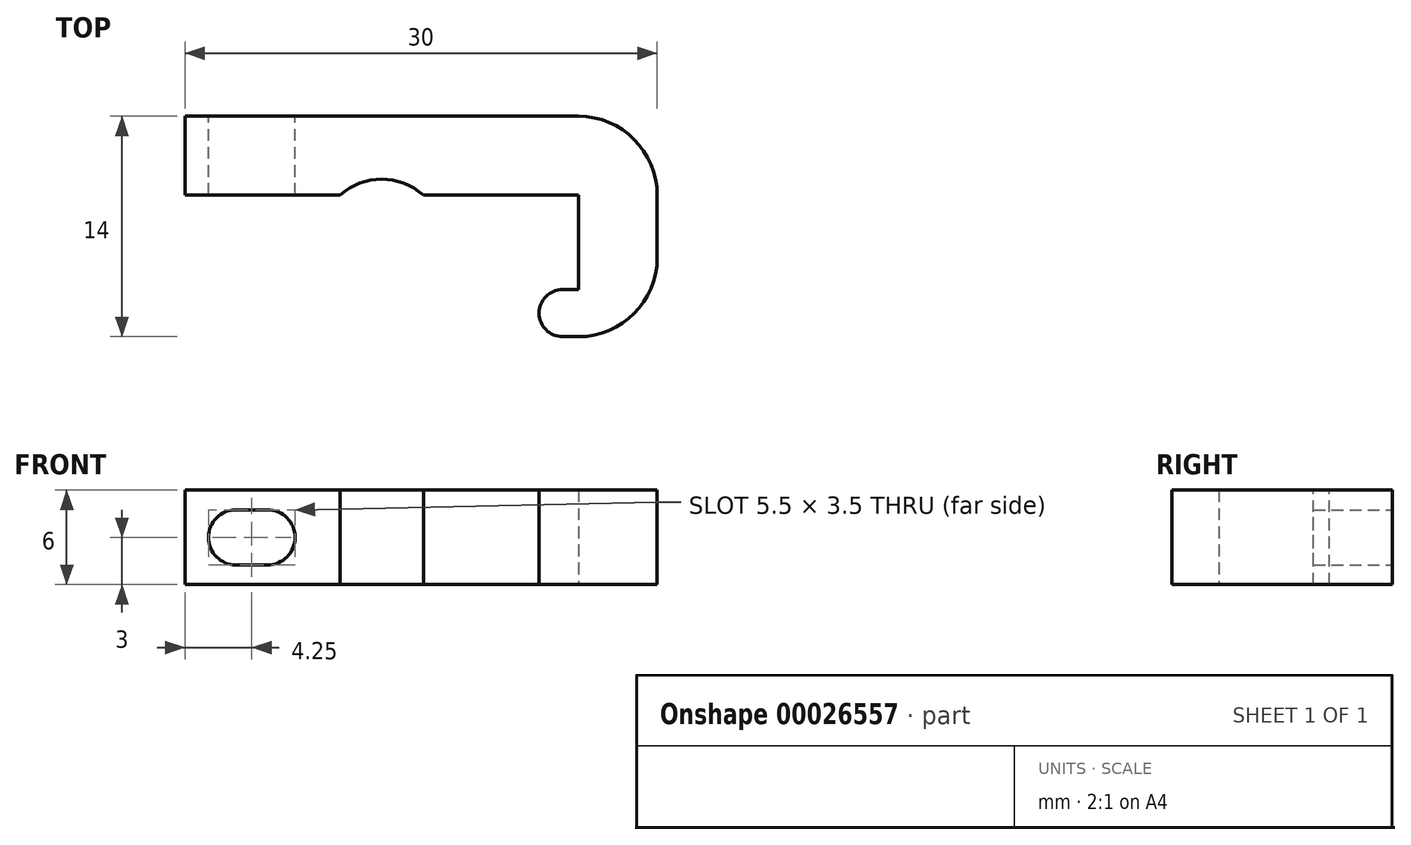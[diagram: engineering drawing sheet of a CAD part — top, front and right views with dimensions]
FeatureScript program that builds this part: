
annotation { "Feature Type Name" : "Feature", "Feature Type Description" : "" }
export const myFeature = defineFeature(function(context is Context, id is Id, definition is map)
    precondition{}
    {
        {
            var Q0;
            Q0=qCreatedBy(makeId("Top.planeOp"),FACE);
            var sketch = newSketch(context, id + "F0", { "sketchPlane" : qUnion([Q0])});
            skLineSegment(sketch, "E0", {"start": v(0, 0) * mm, "end": v(5, 0) * mm});
            skLineSegment(sketch, "E1", {"start": v(5, 0) * mm, "end": v(5, 14) * mm});
            skLineSegment(sketch, "E2", {"start": v(5, 14) * mm, "end": v(-25, 14) * mm});
            skLineSegment(sketch, "E3", {"start": v(-25, 14) * mm, "end": v(-25, 9) * mm});
            skLineSegment(sketch, "E4", {"start": v(-25, 9) * mm, "end": v(0, 9) * mm});
            skLineSegment(sketch, "E5", {"start": v(0, 9) * mm, "end": v(0, 3) * mm});
            skLineSegment(sketch, "E6", {"start": v(0, 3) * mm, "end": v(-1, 3) * mm});
            skLineSegment(sketch, "E7", {"start": v(0, 0) * mm, "end": v(-1, 0) * mm});
            skArc(sketch, "E8", {"start": v(-1, 3) * mm, "mid": v(-2.5, 1.5) * mm, "end": v(-1, 0) * mm});
            skSolve(sketch);
        }
        {
            var Q0;
            Q0=qSketchRegion(id+"F0",true);
            extrude(context, id + "F1", {"entities" : qUnion([Q0]), "depth" : 6 * mm});
        }
        {
            var Q0;
            Q0=makeQuery(id+"F1.opExtrude","SWEPT_FACE",FACE,{"disambiguationData":[OSD([sQuery(id+"F0.wireOp",EDGE,"E2")])]});
            var sketch = newSketch(context, id + "F2", { "sketchPlane" : qUnion([Q0])});
            skCircle(sketch, "E9", {"center": v(21.75, 3) * mm, "radius": 1.75 * mm});
            skLineSegment(sketch, "E10", {"start": v(21.75, 6) * mm, "end": v(21.75, 0) * mm});
            skCircle(sketch, "E11", {"center": v(19.75, 3) * mm, "radius": 1.75 * mm});
            skLineSegment(sketch, "E12", {"start": v(19.75, 4.75) * mm, "end": v(21.75, 4.75) * mm});
            skLineSegment(sketch, "E13", {"start": v(19.75, 1.25) * mm, "end": v(21.75, 1.25) * mm});
            skSolve(sketch);
        }
        {
            var Q0;
            Q0=qSketchRegion(id+"F2",true);
            var Q1;
            {var subQ0=sQuery(id+"F2.wireOp",EDGE,"E11");var subQ1=sQuery(id+"F2.wireOp",EDGE,"E9");var subQ3=makeQuery(id+"F2.imprint","INTERSECT",VERTEX,{"disambiguationData":[OD(0.0)],"derivedFrom":[subQ1,subQ0]});Q1=makeQuery(id+"F2.imprint","IMPRINT",FACE,{"disambiguationData":[TD([[makeQuery(id+"F2.imprint","IMPRINT",EDGE,{"disambiguationData":[TD([[subQ3,-1.0]])],"derivedFrom":subQ1}),1.0]])]});}
            extrude(context, id + "F3", {"entities" : qUnion([Q0, Q1]), "operationType" : NewBodyOperationType.REMOVE, "oppositeDirection" : true, "depth" : 25 * mm});
        }
        {
            var Q0;
            Q0=makeQuery(id+"F1.opExtrude","SWEPT_EDGE",EDGE,{"disambiguationData":[OSD([sQuery(id+"F0.wireOp",EDGE,"E1"),sQuery(id+"F0.wireOp",EDGE,"E2")])]});
            var Q1;
            Q1=makeQuery(id+"F1.opExtrude","SWEPT_EDGE",EDGE,{"disambiguationData":[OSD([sQuery(id+"F0.wireOp",EDGE,"E0"),sQuery(id+"F0.wireOp",EDGE,"E1")])]});
            fillet(context, id + "F4", {"entities" : qUnion([Q0, Q1]), "radius" : 5 * mm, "tangentPropagation" : true, "allowEdgeOverflow" : false});
        }
        {
            var Q0;
            Q0=makeQuery(id+"F1.opExtrude","CAP_FACE",FACE,{"disambiguationData":[OSD([sQuery(id+"F0.wireOp",EDGE,"E0"),sQuery(id+"F0.wireOp",EDGE,"E1"),sQuery(id+"F0.wireOp",EDGE,"E2"),sQuery(id+"F0.wireOp",EDGE,"E3"),sQuery(id+"F0.wireOp",EDGE,"E4"),sQuery(id+"F0.wireOp",EDGE,"E5"),sQuery(id+"F0.wireOp",EDGE,"E6"),sQuery(id+"F0.wireOp",EDGE,"E7"),sQuery(id+"F0.wireOp",EDGE,"E8")])],"isStart":false});
            var sketch = newSketch(context, id + "F5", { "sketchPlane" : qUnion([Q0])});
            skArc(sketch, "E14", {"start": v(-9.85, 9) * mm, "mid": v(-12.5, 10) * mm, "end": v(-15.14, 9) * mm});
            skLineSegment(sketch, "E15", {"start": v(-12.5, 9) * mm, "end": v(-12.5, 2.76) * mm, "construction": true});
            skLineSegment(sketch, "E16", {"start": v(-15.14, 9) * mm, "end": v(-9.85, 9) * mm});
            skSolve(sketch);
        }
        {
            var Q0;
            Q0=makeQuery(id+"F5.imprint","IMPRINT",FACE,{"disambiguationData":[TD([[makeQuery(id+"F5.imprint","IMPRINT",EDGE,{"derivedFrom":sQuery(id+"F5.wireOp",EDGE,"E14")}),1.0]])]});
            extrude(context, id + "F6", {"entities" : qUnion([Q0]), "operationType" : NewBodyOperationType.REMOVE, "endBound" : BoundingType.UP_TO_NEXT, "oppositeDirection" : true, "depth" : 25 * mm});
        }
    });
